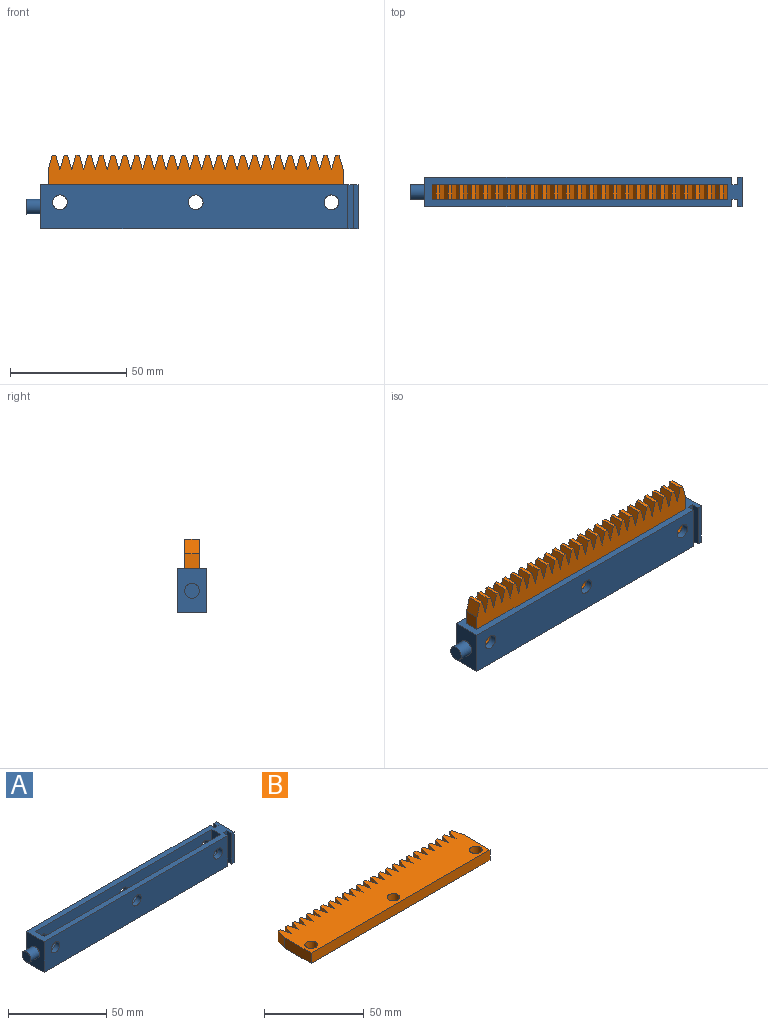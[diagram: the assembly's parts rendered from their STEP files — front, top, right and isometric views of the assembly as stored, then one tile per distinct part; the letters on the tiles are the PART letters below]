
ASSEMBLY  parts=2 mates=1
PART A: 27 faces, bbox 142.9x12.7x19.1 mm
  f0: plane 132.08x19.05mm, normal (0,-1,0), area 2421.1mm2, adj f4,f5,f10,f11,f12,f14,f24
  f1: plane 132.08x19.05mm, normal (0,1,0), area 2421.1mm2, adj f4,f5,f7,f8,f9,f22,f24
  f2: plane 127x12.7mm, normal (0,1,0), area 1517.9mm2, adj f4,f6,f10,f11,f12,f13,f23
  f3: plane 127x12.7mm, normal (0,-1,0), area 1517.9mm2, adj f4,f6,f7,f8,f9,f13,f23
  f4: plane 136.53x12.7mm, normal (0,0,1), area 911.3mm2, adj f0,f1,f2,f3,f13,f14,f15,f16
  f5: plane 136.53x12.7mm, normal (0,0,-1), area 1717.7mm2, adj f0,f1,f14,f15,f16,f17,f18,f19
  f6: plane 127x6.35mm, normal (0,0,1), area 806.5mm2, adj f2,f3,f13,f23
  f7: cylinder r=3.17mm len=6.35mm, axis (0,-1,0), area 63.3mm2, adj f1,f3
  f8: cylinder r=3.17mm len=6.35mm, axis (0,-1,0), area 63.3mm2, adj f1,f3
  f9: cylinder r=3.17mm len=6.35mm, axis (0,-1,0), area 63.3mm2, adj f1,f3
  f10: cylinder r=3.17mm len=6.35mm, axis (0,-1,0), area 63.3mm2, adj f0,f2
  f11: cylinder r=3.17mm len=6.35mm, axis (0,-1,0), area 63.3mm2, adj f0,f2
  f12: cylinder r=3.17mm len=6.35mm, axis (0,-1,0), area 63.3mm2, adj f0,f2
  f13: plane 12.7x6.35mm, normal (-1,0,0), area 80.6mm2, adj f2,f3,f4,f6
  f14: plane 19.05x3.18mm, normal (1,0,0), area 60.5mm2, adj f0,f4,f5,f15
  f15: plane 19.05x2.54mm, normal (0,-1,0), area 48.4mm2, adj f4,f5,f14,f16
  f16: plane 19.05x3.18mm, normal (-1,0,0), area 60.5mm2, adj f4,f5,f15,f17
  f17: plane 19.05x1.91mm, normal (0,-1,0), area 36.3mm2, adj f4,f5,f16,f18
  f18: plane 19.05x12.7mm, normal (1,0,0), area 241.9mm2, adj f4,f5,f17,f19
  f19: plane 19.05x1.91mm, normal (0,1,0), area 36.3mm2, adj f4,f5,f18,f20
  f20: plane 19.05x3.18mm, normal (-1,0,0), area 60.5mm2, adj f4,f5,f19,f21
  f21: plane 19.05x2.54mm, normal (0,1,0), area 48.4mm2, adj f4,f5,f20,f22
  f22: plane 19.05x3.18mm, normal (1,0,0), area 60.5mm2, adj f1,f4,f5,f21
  f23: plane 12.7x6.35mm, normal (1,0,0), area 80.6mm2, adj f2,f3,f4,f6
  f24: plane 19.05x12.7mm, normal (-1,0,0), area 210.3mm2, adj f0,f1,f4,f5,f25
  f25: cylinder r=3.17mm len=6.35mm, axis (1,0,0), area 126.7mm2, adj f24,f26
  f26: plane 6.35x6.35mm, normal (-1,0,0), area 31.7mm2, adj f25
PART B: 83 faces, bbox 127x25.4x6.4 mm
  f0: plane 127x25.4mm, normal (0,0,1), area 2848.5mm2, adj f2,f3,f4,f5,f6,f7,f8,f9
  f1: plane 127x25.4mm, normal (0,0,-1), area 2848.5mm2, adj f2,f3,f4,f5,f6,f7,f8,f9
  f2: plane 6.35x6.35mm, normal (-0.96,0.27,0), area 41.9mm2, adj f0,f1,f3,f79
  f3: plane 6.35x6.35mm, normal (0.96,0.27,0), area 41.9mm2, adj f0,f1,f2,f4
  f4: plane 6.35x1.52mm, normal (0,1,0), area 9.7mm2, adj f0,f1,f3,f5
  f5: plane 6.35x6.35mm, normal (-0.96,0.27,0), area 41.9mm2, adj f0,f1,f4,f6
  f6: plane 6.35x6.35mm, normal (0.96,0.27,0), area 41.9mm2, adj f0,f1,f5,f7
  f7: plane 6.35x1.52mm, normal (0,1,0), area 9.7mm2, adj f0,f1,f6,f8
  f8: plane 6.35x6.35mm, normal (-0.96,0.27,0), area 41.9mm2, adj f0,f1,f7,f9
  f9: plane 6.35x6.35mm, normal (0.96,0.27,0), area 41.9mm2, adj f0,f1,f8,f10
  f10: plane 6.35x1.52mm, normal (0,1,0), area 9.7mm2, adj f0,f1,f9,f11
  f11: plane 6.35x6.35mm, normal (-0.96,0.27,0), area 41.9mm2, adj f0,f1,f10,f12
  f12: plane 6.35x6.35mm, normal (0.96,0.27,0), area 41.9mm2, adj f0,f1,f11,f13
  f13: plane 6.35x1.52mm, normal (0,1,0), area 9.7mm2, adj f0,f1,f12,f14
  f14: plane 6.35x6.35mm, normal (-0.96,0.27,0), area 41.9mm2, adj f0,f1,f13,f15
  f15: plane 6.35x6.35mm, normal (0.96,0.27,0), area 41.9mm2, adj f0,f1,f14,f16
  f16: plane 6.35x1.52mm, normal (0,1,0), area 9.7mm2, adj f0,f1,f15,f17
  f17: plane 6.35x6.35mm, normal (-0.96,0.27,0), area 41.9mm2, adj f0,f1,f16,f18
  f18: plane 6.35x6.35mm, normal (0.96,0.27,0), area 41.9mm2, adj f0,f1,f17,f19
  f19: plane 6.35x1.52mm, normal (0,1,0), area 9.7mm2, adj f0,f1,f18,f20
  f20: plane 6.35x6.35mm, normal (-0.96,0.27,0), area 41.9mm2, adj f0,f1,f19,f21
  f21: plane 6.35x6.35mm, normal (0.96,0.27,0), area 41.9mm2, adj f0,f1,f20,f22
  f22: plane 6.35x1.52mm, normal (0,1,0), area 9.7mm2, adj f0,f1,f21,f23
  f23: plane 6.35x6.35mm, normal (-0.96,0.27,0), area 41.9mm2, adj f0,f1,f22,f24
  f24: plane 6.35x6.35mm, normal (0.96,0.27,0), area 41.9mm2, adj f0,f1,f23,f25
  f25: plane 6.35x1.52mm, normal (0,1,0), area 9.7mm2, adj f0,f1,f24,f26
  f26: plane 6.35x6.35mm, normal (-0.96,0.27,0), area 41.9mm2, adj f0,f1,f25,f27
  f27: plane 6.35x6.35mm, normal (0.96,0.27,0), area 41.9mm2, adj f0,f1,f26,f28
  f28: plane 6.35x1.52mm, normal (0,1,0), area 9.7mm2, adj f0,f1,f27,f29
  f29: plane 6.35x6.35mm, normal (-0.96,0.27,0), area 41.9mm2, adj f0,f1,f28,f30
  f30: plane 6.35x6.35mm, normal (0.96,0.27,0), area 41.9mm2, adj f0,f1,f29,f31
  f31: plane 6.35x1.52mm, normal (0,1,0), area 9.7mm2, adj f0,f1,f30,f32
  f32: plane 6.35x6.35mm, normal (-0.96,0.27,0), area 41.9mm2, adj f0,f1,f31,f33
  f33: plane 19.05x6.35mm, normal (-1,0,0), area 121mm2, adj f0,f1,f32,f34
  f34: plane 127x6.35mm, normal (0,-1,0), area 806.5mm2, adj f0,f1,f33,f35
  f35: plane 19.05x6.35mm, normal (1,0,0), area 121mm2, adj f0,f1,f34,f36
  f36: plane 6.35x6.35mm, normal (0.96,0.27,0), area 41.9mm2, adj f0,f1,f35,f37
  f37: plane 6.35x1.52mm, normal (0,1,0), area 9.7mm2, adj f0,f1,f36,f38
  f38: plane 6.35x6.35mm, normal (-0.96,0.27,0), area 41.9mm2, adj f0,f1,f37,f39
  f39: plane 6.35x6.35mm, normal (0.96,0.27,0), area 41.9mm2, adj f0,f1,f38,f40
  f40: plane 6.35x1.52mm, normal (0,1,0), area 9.7mm2, adj f0,f1,f39,f41
  f41: plane 6.35x6.35mm, normal (-0.96,0.27,0), area 41.9mm2, adj f0,f1,f40,f42
  f42: plane 6.35x6.35mm, normal (0.96,0.27,0), area 41.9mm2, adj f0,f1,f41,f43
  f43: plane 6.35x1.52mm, normal (0,1,0), area 9.7mm2, adj f0,f1,f42,f44
  f44: plane 6.35x6.35mm, normal (-0.96,0.27,0), area 41.9mm2, adj f0,f1,f43,f45
  f45: plane 6.35x6.35mm, normal (0.96,0.27,0), area 41.9mm2, adj f0,f1,f44,f46
  f46: plane 6.35x1.52mm, normal (0,1,0), area 9.7mm2, adj f0,f1,f45,f47
  f47: plane 6.35x6.35mm, normal (-0.96,0.27,0), area 41.9mm2, adj f0,f1,f46,f48
  f48: plane 6.35x6.35mm, normal (0.96,0.27,0), area 41.9mm2, adj f0,f1,f47,f49
  f49: plane 6.35x1.52mm, normal (0,1,0), area 9.7mm2, adj f0,f1,f48,f50
  f50: plane 6.35x6.35mm, normal (-0.96,0.27,0), area 41.9mm2, adj f0,f1,f49,f51
  f51: plane 6.35x6.35mm, normal (0.96,0.27,0), area 41.9mm2, adj f0,f1,f50,f52
  f52: plane 6.35x1.52mm, normal (0,1,0), area 9.7mm2, adj f0,f1,f51,f53
  f53: plane 6.35x6.35mm, normal (-0.96,0.27,0), area 41.9mm2, adj f0,f1,f52,f54
  f54: plane 6.35x6.35mm, normal (0.96,0.27,0), area 41.9mm2, adj f0,f1,f53,f55
  f55: plane 6.35x1.52mm, normal (0,1,0), area 9.7mm2, adj f0,f1,f54,f56
  f56: plane 6.35x6.35mm, normal (-0.96,0.27,0), area 41.9mm2, adj f0,f1,f55,f57
  f57: plane 6.35x6.35mm, normal (0.96,0.27,0), area 41.9mm2, adj f0,f1,f56,f58
  f58: plane 6.35x1.52mm, normal (0,1,0), area 9.7mm2, adj f0,f1,f57,f59
  f59: plane 6.35x6.35mm, normal (-0.96,0.27,0), area 41.9mm2, adj f0,f1,f58,f60
  f60: plane 6.35x6.35mm, normal (0.96,0.27,0), area 41.9mm2, adj f0,f1,f59,f61
  f61: plane 6.35x1.52mm, normal (0,1,0), area 9.7mm2, adj f0,f1,f60,f62
  f62: plane 6.35x6.35mm, normal (-0.96,0.27,0), area 41.9mm2, adj f0,f1,f61,f63
  f63: plane 6.35x6.35mm, normal (0.96,0.27,0), area 41.9mm2, adj f0,f1,f62,f64
  f64: plane 6.35x1.52mm, normal (0,1,0), area 9.7mm2, adj f0,f1,f63,f65
  f65: plane 6.35x6.35mm, normal (-0.96,0.27,0), area 41.9mm2, adj f0,f1,f64,f66
  f66: plane 6.35x6.35mm, normal (0.96,0.27,0), area 41.9mm2, adj f0,f1,f65,f67
  f67: plane 6.35x1.52mm, normal (0,1,0), area 9.7mm2, adj f0,f1,f66,f68
  f68: plane 6.35x6.35mm, normal (-0.96,0.27,0), area 41.9mm2, adj f0,f1,f67,f69
  f69: plane 6.35x6.35mm, normal (0.96,0.27,0), area 41.9mm2, adj f0,f1,f68,f70
  f70: plane 6.35x1.52mm, normal (0,1,0), area 9.7mm2, adj f0,f1,f69,f71
  f71: plane 6.35x6.35mm, normal (-0.96,0.27,0), area 41.9mm2, adj f0,f1,f70,f72
  f72: plane 6.35x6.35mm, normal (0.96,0.27,0), area 41.9mm2, adj f0,f1,f71,f73
  f73: plane 6.35x1.52mm, normal (0,1,0), area 9.7mm2, adj f0,f1,f72,f74
  f74: plane 6.35x6.35mm, normal (-0.96,0.27,0), area 41.9mm2, adj f0,f1,f73,f75
  f75: plane 6.35x6.35mm, normal (0.96,0.27,0), area 41.9mm2, adj f0,f1,f74,f76
  f76: plane 6.35x1.52mm, normal (0,1,0), area 9.7mm2, adj f0,f1,f75,f77
  f77: plane 6.35x6.35mm, normal (-0.96,0.27,0), area 41.9mm2, adj f0,f1,f76,f78
  f78: plane 6.35x6.35mm, normal (0.96,0.27,0), area 41.9mm2, adj f0,f1,f77,f79
  f79: plane 6.35x1.52mm, normal (0,1,0), area 9.7mm2, adj f0,f1,f2,f78
  f80: cylinder r=3.17mm len=6.35mm, axis (0,0,1), area 126.7mm2, adj f0,f1
  f81: cylinder r=3.17mm len=6.35mm, axis (0,0,1), area 126.7mm2, adj f0,f1
  f82: cylinder r=3.17mm len=6.35mm, axis (0,0,1), area 126.7mm2, adj f0,f1
PLACE A t=(84.81,16.69,-54.76)mm
PLACE B rot(axis=(1,0,0),90deg) t=(84.81,13.52,-45.24)mm
MATE fastened B.f34 <-> A.f6  axis (0,0,-1) through (84.81,10.34,-57.94)mm
